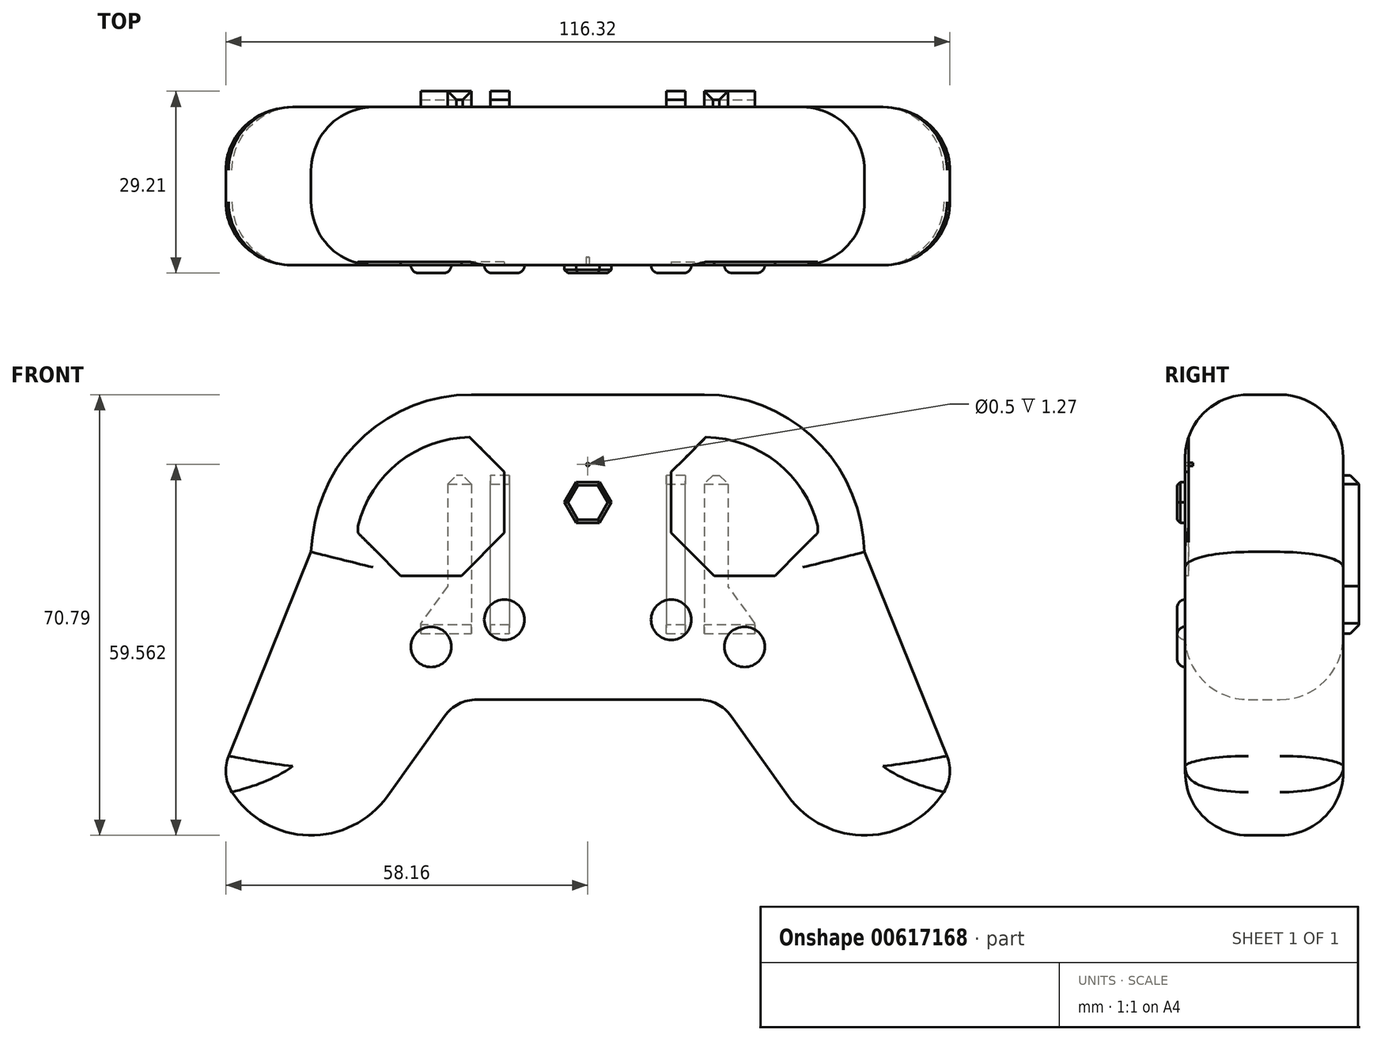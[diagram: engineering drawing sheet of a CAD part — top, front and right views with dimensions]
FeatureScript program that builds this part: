
annotation { "Feature Type Name" : "Feature", "Feature Type Description" : "" }
export const myFeature = defineFeature(function(context is Context, id is Id, definition is map)
    precondition{}
    {
        {
            var Q0;
            Q0=qCreatedBy(makeId("Front.planeOp"),FACE);
            var sketch = newSketch(context, id + "F0", { "sketchPlane" : qUnion([Q0])});
            skLineSegment(sketch, "E0", {"start": v(-44.45, 0) * mm, "end": v(44.45, 0) * mm});
            skLineSegment(sketch, "E1", {"start": v(44.45, 0) * mm, "end": v(44.45, -30.45) * mm, "construction": true});
            skLineSegment(sketch, "E2", {"start": v(-44.45, 0) * mm, "end": v(-57.7, -32.78) * mm});
            skLineSegment(sketch, "E3", {"start": v(44.45, 0) * mm, "end": v(57.7, -32.78) * mm});
            skLineSegment(sketch, "E4", {"start": v(-44.45, -30.45) * mm, "end": v(-44.45, 0) * mm, "construction": true});
            skArc(sketch, "E5", {"start": v(-57.15, -38.58) * mm, "mid": v(-44.84, -45.53) * mm, "end": v(-32.18, -39.22) * mm});
            skArc(sketch, "E6", {"start": v(32.18, -39.22) * mm, "mid": v(44.84, -45.53) * mm, "end": v(57.15, -38.58) * mm});
            skLineSegment(sketch, "E7", {"start": v(32.18, -39.22) * mm, "end": v(23, -26.38) * mm});
            skLineSegment(sketch, "E8", {"start": v(-32.18, -39.22) * mm, "end": v(-23, -26.38) * mm});
            skPoint(sketch, "E9.visualSharp", {"position": v(-58.72, -35.33) * mm});
            skArc(sketch, "E9.filletArc", {"start": v(-57.7, -32.78) * mm, "mid": v(-58.13, -35.74) * mm, "end": v(-57.15, -38.58) * mm});
            skPoint(sketch, "E10.visualSharp", {"position": v(58.72, -35.33) * mm});
            skArc(sketch, "E10.filletArc", {"start": v(57.15, -38.58) * mm, "mid": v(58.13, -35.74) * mm, "end": v(57.7, -32.78) * mm});
            skLineSegment(sketch, "E11", {"start": v(-17.83, -23.72) * mm, "end": v(17.83, -23.72) * mm});
            skPoint(sketch, "E12.visualSharp", {"position": v(-21.1, -23.72) * mm});
            skArc(sketch, "E12.filletArc", {"start": v(-17.83, -23.72) * mm, "mid": v(-20.74, -24.43) * mm, "end": v(-23, -26.38) * mm});
            skPoint(sketch, "E13.visualSharp", {"position": v(21.1, -23.72) * mm});
            skArc(sketch, "E13.filletArc", {"start": v(23, -26.38) * mm, "mid": v(20.74, -24.43) * mm, "end": v(17.83, -23.72) * mm});
            skLineSegment(sketch, "E14", {"start": v(-44.45, 0) * mm, "end": v(-44.2, 2.29) * mm});
            skLineSegment(sketch, "E15", {"start": v(44.45, 0) * mm, "end": v(44.2, 2.29) * mm});
            skLineSegment(sketch, "E16", {"start": v(-18.7, 25.26) * mm, "end": v(18.7, 25.26) * mm});
            skPoint(sketch, "E17.visualSharp", {"position": v(-41.8, 25.26) * mm});
            skArc(sketch, "E17.filletArc", {"start": v(-18.7, 25.26) * mm, "mid": v(-35.86, 18.67) * mm, "end": v(-44.2, 2.29) * mm});
            skPoint(sketch, "E18.visualSharp", {"position": v(41.8, 25.26) * mm});
            skArc(sketch, "E18.filletArc", {"start": v(44.2, 2.29) * mm, "mid": v(35.86, 18.67) * mm, "end": v(18.7, 25.26) * mm});
            skSolve(sketch);
        }
        {
            var Q0;
            Q0=makeQuery(id+"F0.imprint","IMPRINT",FACE,{"disambiguationData":[TD([[makeQuery(id+"F0.imprint","IMPRINT",EDGE,{"derivedFrom":sQuery(id+"F0.wireOp",EDGE,"E0")}),-1.0]])]});
            var Q1;
            Q1=makeQuery(id+"F0.imprint","IMPRINT",FACE,{"disambiguationData":[TD([[makeQuery(id+"F0.imprint","IMPRINT",EDGE,{"derivedFrom":sQuery(id+"F0.wireOp",EDGE,"E0")}),1.0]])]});
            extrude(context, id + "F1", {"entities" : qUnion([Q0, Q1]), "depth" : 25.4 * mm, "offsetDistance" : 25.4 * mm});
        }
        {
            var Q0;
            Q0=makeQuery(id+"F1.opExtrude","CAP_FACE",FACE,{"disambiguationData":[OSD([sQuery(id+"F0.wireOp",EDGE,"E2"),sQuery(id+"F0.wireOp",EDGE,"E3"),sQuery(id+"F0.wireOp",EDGE,"E5"),sQuery(id+"F0.wireOp",EDGE,"E6"),sQuery(id+"F0.wireOp",EDGE,"E7"),sQuery(id+"F0.wireOp",EDGE,"E8"),sQuery(id+"F0.wireOp",EDGE,"E9.filletArc"),sQuery(id+"F0.wireOp",EDGE,"E10.filletArc"),sQuery(id+"F0.wireOp",EDGE,"E11"),sQuery(id+"F0.wireOp",EDGE,"E12.filletArc"),sQuery(id+"F0.wireOp",EDGE,"E13.filletArc"),sQuery(id+"F0.wireOp",EDGE,"E14"),sQuery(id+"F0.wireOp",EDGE,"E15"),sQuery(id+"F0.wireOp",EDGE,"E16"),sQuery(id+"F0.wireOp",EDGE,"E17.filletArc"),sQuery(id+"F0.wireOp",EDGE,"E18.filletArc")])],"isStart":false});
            var sketch = newSketch(context, id + "F2", { "sketchPlane" : qUnion([Q0])});
            skArc(sketch, "E19.0.0", {"start": v(-23, -26.38) * mm, "mid": v(-20.74, -24.43) * mm, "end": v(-17.83, -23.72) * mm});
            skLineSegment(sketch, "E19.0.1", {"start": v(-17.83, -23.72) * mm, "end": v(17.83, -23.72) * mm});
            skArc(sketch, "E19.0.2", {"start": v(17.83, -23.72) * mm, "mid": v(20.74, -24.43) * mm, "end": v(23, -26.38) * mm});
            skLineSegment(sketch, "E19.0.3", {"start": v(23, -26.38) * mm, "end": v(32.18, -39.22) * mm});
            skArc(sketch, "E19.0.4", {"start": v(32.18, -39.22) * mm, "mid": v(44.84, -45.53) * mm, "end": v(57.15, -38.58) * mm});
            skArc(sketch, "E19.0.5", {"start": v(57.15, -38.58) * mm, "mid": v(58.13, -35.74) * mm, "end": v(57.7, -32.78) * mm});
            skLineSegment(sketch, "E19.0.6", {"start": v(57.7, -32.78) * mm, "end": v(44.45, 0) * mm});
            skLineSegment(sketch, "E19.0.7", {"start": v(44.45, 0) * mm, "end": v(44.2, 2.29) * mm});
            skArc(sketch, "E19.0.8", {"start": v(44.2, 2.29) * mm, "mid": v(35.86, 18.67) * mm, "end": v(18.7, 25.26) * mm});
            skLineSegment(sketch, "E19.0.9", {"start": v(18.7, 25.26) * mm, "end": v(-18.7, 25.26) * mm});
            skArc(sketch, "E19.0.10", {"start": v(-18.7, 25.26) * mm, "mid": v(-35.86, 18.67) * mm, "end": v(-44.2, 2.29) * mm});
            skLineSegment(sketch, "E19.0.11", {"start": v(-44.2, 2.29) * mm, "end": v(-44.45, 0) * mm});
            skLineSegment(sketch, "E19.0.12", {"start": v(-44.45, 0) * mm, "end": v(-57.7, -32.78) * mm});
            skArc(sketch, "E19.0.13", {"start": v(-57.7, -32.78) * mm, "mid": v(-58.13, -35.74) * mm, "end": v(-57.15, -38.58) * mm});
            skArc(sketch, "E19.0.14", {"start": v(-57.15, -38.58) * mm, "mid": v(-44.84, -45.53) * mm, "end": v(-32.18, -39.22) * mm});
            skLineSegment(sketch, "E19.0.15", {"start": v(-32.18, -39.22) * mm, "end": v(-23, -26.38) * mm});
            skLineSegment(sketch, "E20", {"start": v(-25.17, 24.43) * mm, "end": v(-25.17, 19.73) * mm});
            skLineSegment(sketch, "E21", {"start": v(-44.45, 0) * mm, "end": v(44.45, 0) * mm});
            skLineSegment(sketch, "E22", {"start": v(25.17, 24.43) * mm, "end": v(25.17, 19.73) * mm});
            skLineSegment(sketch, "E23.0", {"start": v(-30.05, 19.73) * mm, "end": v(-20.3, 19.73) * mm});
            skLineSegment(sketch, "E23.1", {"start": v(-20.3, 19.73) * mm, "end": v(-13.4, 12.83) * mm});
            skLineSegment(sketch, "E23.2", {"start": v(-13.4, 12.83) * mm, "end": v(-13.4, 3.08) * mm});
            skLineSegment(sketch, "E23.3", {"start": v(-13.4, 3.08) * mm, "end": v(-20.3, -3.82) * mm});
            skLineSegment(sketch, "E23.4", {"start": v(-20.3, -3.82) * mm, "end": v(-30.05, -3.82) * mm});
            skLineSegment(sketch, "E23.5", {"start": v(-30.05, -3.82) * mm, "end": v(-36.95, 3.08) * mm});
            skLineSegment(sketch, "E23.6", {"start": v(-36.95, 3.08) * mm, "end": v(-36.95, 12.83) * mm});
            skLineSegment(sketch, "E23.7", {"start": v(-36.95, 12.83) * mm, "end": v(-30.05, 19.73) * mm});
            skPoint(sketch, "E23.0.midPoint", {"position": v(-25.17, 19.73) * mm});
            skPoint(sketch, "E24.cCircle.centerSnap0", {"position": v(-13.4, 7.95) * mm});
            skLineSegment(sketch, "E24.0", {"start": v(20.3, 19.73) * mm, "end": v(30.05, 19.73) * mm});
            skLineSegment(sketch, "E24.1", {"start": v(30.05, 19.73) * mm, "end": v(36.95, 12.83) * mm});
            skLineSegment(sketch, "E24.2", {"start": v(36.95, 12.83) * mm, "end": v(36.95, 3.08) * mm});
            skLineSegment(sketch, "E24.3", {"start": v(36.95, 3.08) * mm, "end": v(30.05, -3.82) * mm});
            skLineSegment(sketch, "E24.4", {"start": v(30.05, -3.82) * mm, "end": v(20.3, -3.82) * mm});
            skLineSegment(sketch, "E24.5", {"start": v(20.3, -3.82) * mm, "end": v(13.4, 3.08) * mm});
            skLineSegment(sketch, "E24.6", {"start": v(13.4, 3.08) * mm, "end": v(13.4, 12.83) * mm});
            skLineSegment(sketch, "E24.7", {"start": v(13.4, 12.83) * mm, "end": v(20.3, 19.73) * mm});
            skPoint(sketch, "E24.0.midPoint", {"position": v(25.17, 19.73) * mm});
            skLineSegment(sketch, "E25", {"start": v(-20.3, -3.82) * mm, "end": v(-30.05, 19.73) * mm});
            skLineSegment(sketch, "E26", {"start": v(-30.05, -3.82) * mm, "end": v(-20.3, 19.73) * mm});
            skLineSegment(sketch, "E27", {"start": v(-13.4, 12.83) * mm, "end": v(-36.95, 3.08) * mm});
            skLineSegment(sketch, "E28", {"start": v(-36.95, 12.83) * mm, "end": v(-13.4, 3.08) * mm});
            skLineSegment(sketch, "E29", {"start": v(13.4, 12.83) * mm, "end": v(36.95, 3.08) * mm});
            skLineSegment(sketch, "E30", {"start": v(13.4, 3.08) * mm, "end": v(36.95, 12.83) * mm});
            skLineSegment(sketch, "E31", {"start": v(20.3, 19.73) * mm, "end": v(30.05, -3.82) * mm});
            skLineSegment(sketch, "E32", {"start": v(20.3, -3.82) * mm, "end": v(30.05, 19.73) * mm});
            skLineSegment(sketch, "E33", {"start": v(-13.4, 3.08) * mm, "end": v(-13.4, -10.9) * mm, "construction": true});
            skLineSegment(sketch, "E34", {"start": v(-25.17, -3.82) * mm, "end": v(-25.17, -15.25) * mm, "construction": true});
            skCircle(sketch, "E35", {"center": v(-25.17, -15.25) * mm, "radius": 3.24 * mm});
            skCircle(sketch, "E36", {"center": v(-13.4, -10.9) * mm, "radius": 3.24 * mm});
            skLineSegment(sketch, "E37", {"start": v(13.4, 3.08) * mm, "end": v(13.4, -10.9) * mm, "construction": true});
            skLineSegment(sketch, "E38", {"start": v(25.17, -3.82) * mm, "end": v(25.17, -15.25) * mm, "construction": true});
            skCircle(sketch, "E39", {"center": v(13.4, -10.9) * mm, "radius": 3.24 * mm});
            skCircle(sketch, "E40", {"center": v(25.17, -15.25) * mm, "radius": 3.24 * mm});
            skLineSegment(sketch, "E41", {"start": v(-13.4, 7.95) * mm, "end": v(13.4, 7.95) * mm});
            skCircle(sketch, "E42.cCircle", {"center": v(0, 7.95) * mm, "radius": 3.27 * mm, "construction": true});
            skLineSegment(sketch, "E42.0", {"start": v(-1.89, 11.22) * mm, "end": v(1.89, 11.22) * mm});
            skLineSegment(sketch, "E42.1", {"start": v(1.89, 11.22) * mm, "end": v(3.77, 7.95) * mm});
            skLineSegment(sketch, "E42.2", {"start": v(3.77, 7.95) * mm, "end": v(1.89, 4.69) * mm});
            skLineSegment(sketch, "E42.3", {"start": v(1.89, 4.69) * mm, "end": v(-1.89, 4.69) * mm});
            skLineSegment(sketch, "E42.4", {"start": v(-1.89, 4.69) * mm, "end": v(-3.77, 7.95) * mm});
            skLineSegment(sketch, "E42.5", {"start": v(-3.77, 7.95) * mm, "end": v(-1.89, 11.22) * mm});
            skPoint(sketch, "E42.0.midPoint", {"position": v(0, 11.22) * mm});
            skLineSegment(sketch, "E43", {"start": v(0, 11.22) * mm, "end": v(0, 14.03) * mm});
            skCircle(sketch, "E44", {"center": v(0, 14.03) * mm, "radius": 0.25 * mm});
            skSolve(sketch);
        }
        {
            var Q0;
            Q0=makeQuery(id+"F2.imprint","IMPRINT",FACE,{"disambiguationData":[TD([[makeQuery(id+"F2.imprint","IMPRINT",EDGE,{"derivedFrom":sQuery(id+"F2.wireOp",EDGE,"E35")}),1.0]])]});
            var Q1;
            Q1=makeQuery(id+"F2.imprint","IMPRINT",FACE,{"disambiguationData":[TD([[makeQuery(id+"F2.imprint","IMPRINT",EDGE,{"derivedFrom":sQuery(id+"F2.wireOp",EDGE,"E36")}),1.0]])]});
            var Q2;
            Q2=makeQuery(id+"F2.imprint","IMPRINT",FACE,{"disambiguationData":[TD([[makeQuery(id+"F2.imprint","IMPRINT",EDGE,{"derivedFrom":sQuery(id+"F2.wireOp",EDGE,"E39")}),1.0]])]});
            var Q3;
            Q3=makeQuery(id+"F2.imprint","IMPRINT",FACE,{"disambiguationData":[TD([[makeQuery(id+"F2.imprint","IMPRINT",EDGE,{"derivedFrom":sQuery(id+"F2.wireOp",EDGE,"E40")}),1.0]])]});
            var Q4;
            {var subQ0=sQuery(id+"F2.wireOp",EDGE,"E42.2");Q4=makeQuery(id+"F2.imprint","IMPRINT",FACE,{"disambiguationData":[TD([[makeQuery(id+"F2.imprint","IMPRINT",EDGE,{"derivedFrom":subQ0}),-1.0]])]});}
            var Q5;
            Q5=makeQuery(id+"F2.imprint","IMPRINT",FACE,{"disambiguationData":[TD([[makeQuery(id+"F2.imprint","IMPRINT",EDGE,{"derivedFrom":sQuery(id+"F2.wireOp",EDGE,"E42.0")}),-1.0]])]});
            extrude(context, id + "F3", {"entities" : qUnion([Q0, Q1, Q2, Q3, Q4, Q5]), "depth" : 1.27 * mm, "offsetDistance" : 25.4 * mm});
        }
        {
            var Q0;
            {var subQ0=sQuery(id+"F2.wireOp",EDGE,"E25");var subQ1=sQuery(id+"F2.wireOp",EDGE,"E21");var subQ2=makeQuery(id+"F2.imprint","INTERSECT",VERTEX,{"derivedFrom":[subQ1,subQ0]});Q0=makeQuery(id+"F2.imprint","IMPRINT",FACE,{"disambiguationData":[TD([[makeQuery(id+"F2.imprint","IMPRINT",EDGE,{"disambiguationData":[TD([[subQ2,-1.0]])],"derivedFrom":subQ1}),1.0]])]});}
            var Q1;
            {var subQ0=sQuery(id+"F2.wireOp",EDGE,"E25");var subQ1=sQuery(id+"F2.wireOp",EDGE,"E21");var subQ2=makeQuery(id+"F2.imprint","INTERSECT",VERTEX,{"derivedFrom":[subQ1,subQ0]});Q1=makeQuery(id+"F2.imprint","IMPRINT",FACE,{"disambiguationData":[TD([[makeQuery(id+"F2.imprint","IMPRINT",EDGE,{"disambiguationData":[TD([[subQ2,-1.0]])],"derivedFrom":subQ1}),-1.0]])]});}
            var Q2;
            {var subQ5=sQuery(id+"F2.wireOp",EDGE,"E23.4");Q2=makeQuery(id+"F2.imprint","IMPRINT",FACE,{"disambiguationData":[TD([[makeQuery(id+"F2.imprint","IMPRINT",EDGE,{"derivedFrom":subQ5}),-1.0]])]});}
            var Q3;
            {var subQ0=sQuery(id+"F2.wireOp",EDGE,"E23.5");var subQ1=sQuery(id+"F2.wireOp",EDGE,"E21");var subQ2=makeQuery(id+"F2.imprint","INTERSECT",VERTEX,{"derivedFrom":[subQ1,subQ0]});Q3=makeQuery(id+"F2.imprint","IMPRINT",FACE,{"disambiguationData":[TD([[makeQuery(id+"F2.imprint","IMPRINT",EDGE,{"disambiguationData":[TD([[subQ2,-1.0]])],"derivedFrom":subQ1}),-1.0]])]});}
            var Q4;
            {var subQ0=sQuery(id+"F2.wireOp",EDGE,"E23.5");var subQ1=sQuery(id+"F2.wireOp",EDGE,"E21");var subQ2=makeQuery(id+"F2.imprint","INTERSECT",VERTEX,{"derivedFrom":[subQ1,subQ0]});Q4=makeQuery(id+"F2.imprint","IMPRINT",FACE,{"disambiguationData":[TD([[makeQuery(id+"F2.imprint","IMPRINT",EDGE,{"disambiguationData":[TD([[subQ2,-1.0]])],"derivedFrom":subQ1}),1.0]])]});}
            var Q5;
            {var subQ0=sQuery(id+"F2.wireOp",EDGE,"E23.6");Q5=makeQuery(id+"F2.imprint","IMPRINT",FACE,{"disambiguationData":[TD([[makeQuery(id+"F2.imprint","IMPRINT",EDGE,{"derivedFrom":subQ0}),-1.0]])]});}
            var Q6;
            {var subQ0=sQuery(id+"F2.wireOp",EDGE,"E23.7");Q6=makeQuery(id+"F2.imprint","IMPRINT",FACE,{"disambiguationData":[TD([[makeQuery(id+"F2.imprint","IMPRINT",EDGE,{"derivedFrom":subQ0}),-1.0]])]});}
            var Q7;
            {var subQ0=sQuery(id+"F2.wireOp",EDGE,"E23.0");var subQ1=makeQuery(id+"F2.imprint","INTERSECT",VERTEX,{"derivedFrom":[sQuery(id+"F2.wireOp",EDGE,"E20"),subQ0]});Q7=makeQuery(id+"F2.imprint","IMPRINT",FACE,{"disambiguationData":[TD([[makeQuery(id+"F2.imprint","IMPRINT",EDGE,{"disambiguationData":[TD([[subQ1,1.0]])],"derivedFrom":subQ0}),-1.0]])]});}
            var Q8;
            {var subQ0=sQuery(id+"F2.wireOp",EDGE,"E23.1");Q8=makeQuery(id+"F2.imprint","IMPRINT",FACE,{"disambiguationData":[TD([[makeQuery(id+"F2.imprint","IMPRINT",EDGE,{"derivedFrom":subQ0}),-1.0]])]});}
            var Q9;
            {var subQ1=sQuery(id+"F2.wireOp",EDGE,"E23.2");var subQ3=makeQuery(id+"F2.imprint","INTERSECT",VERTEX,{"derivedFrom":[subQ1,sQuery(id+"F2.wireOp",EDGE,"E41")]});Q9=makeQuery(id+"F2.imprint","IMPRINT",FACE,{"disambiguationData":[TD([[makeQuery(id+"F2.imprint","IMPRINT",EDGE,{"disambiguationData":[TD([[subQ3,1.0]])],"derivedFrom":subQ1}),-1.0]])]});}
            var Q10;
            {var subQ1=sQuery(id+"F2.wireOp",EDGE,"E24.6");var subQ3=makeQuery(id+"F2.imprint","INTERSECT",VERTEX,{"derivedFrom":[subQ1,sQuery(id+"F2.wireOp",EDGE,"E41")]});Q10=makeQuery(id+"F2.imprint","IMPRINT",FACE,{"disambiguationData":[TD([[makeQuery(id+"F2.imprint","IMPRINT",EDGE,{"disambiguationData":[TD([[subQ3,1.0]])],"derivedFrom":subQ1}),-1.0]])]});}
            var Q11;
            {var subQ0=sQuery(id+"F2.wireOp",EDGE,"E24.5");var subQ1=sQuery(id+"F2.wireOp",EDGE,"E21");var subQ2=makeQuery(id+"F2.imprint","INTERSECT",VERTEX,{"derivedFrom":[subQ1,subQ0]});Q11=makeQuery(id+"F2.imprint","IMPRINT",FACE,{"disambiguationData":[TD([[makeQuery(id+"F2.imprint","IMPRINT",EDGE,{"disambiguationData":[TD([[subQ2,-1.0]])],"derivedFrom":subQ1}),1.0]])]});}
            var Q12;
            {var subQ0=sQuery(id+"F2.wireOp",EDGE,"E32");var subQ1=sQuery(id+"F2.wireOp",EDGE,"E21");var subQ2=makeQuery(id+"F2.imprint","INTERSECT",VERTEX,{"derivedFrom":[subQ1,subQ0]});Q12=makeQuery(id+"F2.imprint","IMPRINT",FACE,{"disambiguationData":[TD([[makeQuery(id+"F2.imprint","IMPRINT",EDGE,{"disambiguationData":[TD([[subQ2,-1.0]])],"derivedFrom":subQ1}),1.0]])]});}
            var Q13;
            {var subQ0=sQuery(id+"F2.wireOp",EDGE,"E31");var subQ1=sQuery(id+"F2.wireOp",EDGE,"E21");var subQ2=makeQuery(id+"F2.imprint","INTERSECT",VERTEX,{"derivedFrom":[subQ1,subQ0]});Q13=makeQuery(id+"F2.imprint","IMPRINT",FACE,{"disambiguationData":[TD([[makeQuery(id+"F2.imprint","IMPRINT",EDGE,{"disambiguationData":[TD([[subQ2,-1.0]])],"derivedFrom":subQ1}),1.0]])]});}
            var Q14;
            {var subQ0=sQuery(id+"F2.wireOp",EDGE,"E24.2");Q14=makeQuery(id+"F2.imprint","IMPRINT",FACE,{"disambiguationData":[TD([[makeQuery(id+"F2.imprint","IMPRINT",EDGE,{"derivedFrom":subQ0}),-1.0]])]});}
            var Q15;
            {var subQ0=sQuery(id+"F2.wireOp",EDGE,"E24.1");Q15=makeQuery(id+"F2.imprint","IMPRINT",FACE,{"disambiguationData":[TD([[makeQuery(id+"F2.imprint","IMPRINT",EDGE,{"derivedFrom":subQ0}),-1.0]])]});}
            var Q16;
            {var subQ0=sQuery(id+"F2.wireOp",EDGE,"E24.0");var subQ1=makeQuery(id+"F2.imprint","INTERSECT",VERTEX,{"derivedFrom":[sQuery(id+"F2.wireOp",EDGE,"E22"),subQ0]});Q16=makeQuery(id+"F2.imprint","IMPRINT",FACE,{"disambiguationData":[TD([[makeQuery(id+"F2.imprint","IMPRINT",EDGE,{"disambiguationData":[TD([[subQ1,1.0]])],"derivedFrom":subQ0}),-1.0]])]});}
            var Q17;
            {var subQ0=sQuery(id+"F2.wireOp",EDGE,"E24.7");Q17=makeQuery(id+"F2.imprint","IMPRINT",FACE,{"disambiguationData":[TD([[makeQuery(id+"F2.imprint","IMPRINT",EDGE,{"derivedFrom":subQ0}),-1.0]])]});}
            var Q18;
            {var subQ5=sQuery(id+"F2.wireOp",EDGE,"E24.4");Q18=makeQuery(id+"F2.imprint","IMPRINT",FACE,{"disambiguationData":[TD([[makeQuery(id+"F2.imprint","IMPRINT",EDGE,{"derivedFrom":subQ5}),-1.0]])]});}
            var Q19;
            {var subQ0=sQuery(id+"F2.wireOp",EDGE,"E31");var subQ1=sQuery(id+"F2.wireOp",EDGE,"E21");var subQ2=makeQuery(id+"F2.imprint","INTERSECT",VERTEX,{"derivedFrom":[subQ1,subQ0]});Q19=makeQuery(id+"F2.imprint","IMPRINT",FACE,{"disambiguationData":[TD([[makeQuery(id+"F2.imprint","IMPRINT",EDGE,{"disambiguationData":[TD([[subQ2,-1.0]])],"derivedFrom":subQ1}),-1.0]])]});}
            var Q20;
            {var subQ0=sQuery(id+"F2.wireOp",EDGE,"E24.5");var subQ1=sQuery(id+"F2.wireOp",EDGE,"E21");var subQ2=makeQuery(id+"F2.imprint","INTERSECT",VERTEX,{"derivedFrom":[subQ1,subQ0]});Q20=makeQuery(id+"F2.imprint","IMPRINT",FACE,{"disambiguationData":[TD([[makeQuery(id+"F2.imprint","IMPRINT",EDGE,{"disambiguationData":[TD([[subQ2,-1.0]])],"derivedFrom":subQ1}),-1.0]])]});}
            var Q21;
            {var subQ0=sQuery(id+"F2.wireOp",EDGE,"E26");var subQ1=sQuery(id+"F2.wireOp",EDGE,"E21");var subQ2=makeQuery(id+"F2.imprint","INTERSECT",VERTEX,{"derivedFrom":[subQ1,subQ0]});Q21=makeQuery(id+"F2.imprint","IMPRINT",FACE,{"disambiguationData":[TD([[makeQuery(id+"F2.imprint","IMPRINT",EDGE,{"disambiguationData":[TD([[subQ2,-1.0]])],"derivedFrom":subQ1}),1.0]])]});}
            extrude(context, id + "F4", {"entities" : qUnion([Q0, Q1, Q2, Q3, Q4, Q5, Q6, Q7, Q8, Q9, Q10, Q11, Q12, Q13, Q14, Q15, Q16, Q17, Q18, Q19, Q20, Q21]), "operationType" : NewBodyOperationType.REMOVE, "oppositeDirection" : true, "depth" : 0.56 * mm, "offsetDistance" : 25.4 * mm});
        }
        {
            var Q0;
            Q0=makeQuery(id+"F1.opExtrude","CAP_EDGE",EDGE,{"disambiguationData":[OSD([sQuery(id+"F0.wireOp",EDGE,"E18.filletArc")])],"isStart":false});
            var Q1;
            Q1=makeQuery(id+"F1.opExtrude","CAP_EDGE",EDGE,{"disambiguationData":[OSD([sQuery(id+"F0.wireOp",EDGE,"E3")])],"isStart":false});
            var Q2;
            Q2=makeQuery(id+"F1.opExtrude","CAP_EDGE",EDGE,{"disambiguationData":[OSD([sQuery(id+"F0.wireOp",EDGE,"E18.filletArc")])],"isStart":true});
            var Q3;
            Q3=makeQuery(id+"F1.opExtrude","CAP_EDGE",EDGE,{"disambiguationData":[OSD([sQuery(id+"F0.wireOp",EDGE,"E3")])],"isStart":true});
            fillet(context, id + "F5", {"entities" : qUnion([Q0, Q1, Q2, Q3]), "radius" : 10.16 * mm, "tangentPropagation" : true, "allowEdgeOverflow" : false});
        }
        {
            var Q0;
            Q0=makeQuery(id+"F2.imprint","IMPRINT",FACE,{"disambiguationData":[TD([[makeQuery(id+"F2.imprint","IMPRINT",EDGE,{"derivedFrom":sQuery(id+"F2.wireOp",EDGE,"E44")}),1.0]])]});
            extrude(context, id + "F6", {"entities" : qUnion([Q0]), "operationType" : NewBodyOperationType.REMOVE, "oppositeDirection" : true, "depth" : 1.27 * mm, "offsetDistance" : 25.4 * mm});
        }
        {
            var Q0;
            Q0=makeQuery(id+"F3.opExtrude","CAP_EDGE",EDGE,{"disambiguationData":[OSD([sQuery(id+"F2.wireOp",EDGE,"E36")])],"isStart":false});
            var Q1;
            Q1=makeQuery(id+"F3.opExtrude","CAP_EDGE",EDGE,{"disambiguationData":[OSD([sQuery(id+"F2.wireOp",EDGE,"E35")])],"isStart":false});
            var Q2;
            Q2=makeQuery(id+"F3.opExtrude","CAP_EDGE",EDGE,{"disambiguationData":[OSD([sQuery(id+"F2.wireOp",EDGE,"E39")])],"isStart":false});
            var Q3;
            Q3=makeQuery(id+"F3.opExtrude","CAP_EDGE",EDGE,{"disambiguationData":[OSD([sQuery(id+"F2.wireOp",EDGE,"E40")])],"isStart":false});
            fillet(context, id + "F7", {"entities" : qUnion([Q0, Q1, Q2, Q3]), "radius" : 1.27 * mm, "tangentPropagation" : true, "allowEdgeOverflow" : false});
        }
        {
            var Q0;
            Q0=makeQuery(id+"F3.opExtrude","CAP_EDGE",EDGE,{"disambiguationData":[OSD([sQuery(id+"F2.wireOp",EDGE,"E42.3")])],"isStart":false});
            var Q1;
            Q1=makeQuery(id+"F3.opExtrude","CAP_EDGE",EDGE,{"disambiguationData":[OSD([sQuery(id+"F2.wireOp",EDGE,"E42.2")])],"isStart":false});
            var Q2;
            Q2=makeQuery(id+"F3.opExtrude","CAP_EDGE",EDGE,{"disambiguationData":[OSD([sQuery(id+"F2.wireOp",EDGE,"E42.1")])],"isStart":false});
            var Q3;
            Q3=makeQuery(id+"F3.opExtrude","CAP_EDGE",EDGE,{"disambiguationData":[OSD([sQuery(id+"F2.wireOp",EDGE,"E42.4")])],"isStart":false});
            var Q4;
            Q4=makeQuery(id+"F3.opExtrude","CAP_EDGE",EDGE,{"disambiguationData":[OSD([sQuery(id+"F2.wireOp",EDGE,"E42.5")])],"isStart":false});
            var Q5;
            Q5=makeQuery(id+"F3.opExtrude","CAP_EDGE",EDGE,{"disambiguationData":[OSD([sQuery(id+"F2.wireOp",EDGE,"E42.0")])],"isStart":false});
            chamfer(context, id + "F8", {"entities" : qUnion([Q0, Q1, Q2, Q3, Q4, Q5]), "width" : 0.5 * mm, "tangentPropagation" : true});
        }
        {
            var Q0;
            Q0=makeQuery(id+"F1.opExtrude","CAP_FACE",FACE,{"disambiguationData":[OSD([sQuery(id+"F0.wireOp",EDGE,"E2"),sQuery(id+"F0.wireOp",EDGE,"E3"),sQuery(id+"F0.wireOp",EDGE,"E5"),sQuery(id+"F0.wireOp",EDGE,"E6"),sQuery(id+"F0.wireOp",EDGE,"E7"),sQuery(id+"F0.wireOp",EDGE,"E8"),sQuery(id+"F0.wireOp",EDGE,"E9.filletArc"),sQuery(id+"F0.wireOp",EDGE,"E10.filletArc"),sQuery(id+"F0.wireOp",EDGE,"E11"),sQuery(id+"F0.wireOp",EDGE,"E12.filletArc"),sQuery(id+"F0.wireOp",EDGE,"E13.filletArc"),sQuery(id+"F0.wireOp",EDGE,"E14"),sQuery(id+"F0.wireOp",EDGE,"E15"),sQuery(id+"F0.wireOp",EDGE,"E16"),sQuery(id+"F0.wireOp",EDGE,"E17.filletArc"),sQuery(id+"F0.wireOp",EDGE,"E18.filletArc")])],"isStart":true});
            var sketch = newSketch(context, id + "F9", { "sketchPlane" : qUnion([Q0])});
            skLineSegment(sketch, "E45.0.0", {"start": v(48.27, -36.58) * mm, "end": v(34.5, -2.48) * mm});
            skLineSegment(sketch, "E45.0.1", {"start": v(34.5, -2.48) * mm, "end": v(34.1, 1.23) * mm});
            skArc(sketch, "E45.0.2", {"start": v(34.1, 1.23) * mm, "mid": v(29.06, 11.12) * mm, "end": v(18.7, 15.1) * mm});
            skLineSegment(sketch, "E45.0.3", {"start": v(18.7, 15.1) * mm, "end": v(-18.7, 15.1) * mm});
            skArc(sketch, "E45.0.4", {"start": v(-18.7, 15.1) * mm, "mid": v(-29.06, 11.12) * mm, "end": v(-34.1, 1.23) * mm});
            skLineSegment(sketch, "E45.0.5", {"start": v(-34.1, 1.23) * mm, "end": v(-34.5, -2.48) * mm});
            skLineSegment(sketch, "E45.0.6", {"start": v(-34.5, -2.48) * mm, "end": v(-48.27, -36.58) * mm});
            skArc(sketch, "E45.0.7", {"start": v(-48.27, -36.58) * mm, "mid": v(-46.7, -34.68) * mm, "end": v(-48.6, -33.1) * mm});
            skArc(sketch, "E45.0.8", {"start": v(-48.6, -33.1) * mm, "mid": v(-44.58, -35.37) * mm, "end": v(-40.45, -33.31) * mm});
            skLineSegment(sketch, "E45.0.9", {"start": v(-40.45, -33.31) * mm, "end": v(-31.26, -20.47) * mm});
            skArc(sketch, "E45.0.10", {"start": v(-31.26, -20.47) * mm, "mid": v(-25.39, -15.4) * mm, "end": v(-17.83, -13.56) * mm});
            skLineSegment(sketch, "E45.0.11", {"start": v(-17.83, -13.56) * mm, "end": v(17.83, -13.56) * mm});
            skArc(sketch, "E45.0.12", {"start": v(17.83, -13.56) * mm, "mid": v(25.39, -15.4) * mm, "end": v(31.26, -20.47) * mm});
            skLineSegment(sketch, "E45.0.13", {"start": v(31.26, -20.47) * mm, "end": v(40.45, -33.31) * mm});
            skArc(sketch, "E45.0.14", {"start": v(40.45, -33.31) * mm, "mid": v(44.58, -35.37) * mm, "end": v(48.6, -33.1) * mm});
            skArc(sketch, "E45.0.15", {"start": v(48.6, -33.1) * mm, "mid": v(46.7, -34.68) * mm, "end": v(48.27, -36.58) * mm});
            skLineSegment(sketch, "E46", {"start": v(-18.7, 12.3) * mm, "end": v(-18.7, -13.1) * mm});
            skLineSegment(sketch, "E47", {"start": v(18.7, 12.3) * mm, "end": v(18.7, -13.1) * mm});
            skLineSegment(sketch, "E48", {"start": v(-18.7, 12.3) * mm, "end": v(-22.5, 12.3) * mm});
            skLineSegment(sketch, "E49", {"start": v(-22.5, 12.3) * mm, "end": v(-22.5, -5.47) * mm});
            skLineSegment(sketch, "E50", {"start": v(-18.7, -13.1) * mm, "end": v(-26.82, -13.1) * mm});
            skLineSegment(sketch, "E51", {"start": v(-26.82, -13.1) * mm, "end": v(-26.82, -11.44) * mm});
            skLineSegment(sketch, "E52", {"start": v(-26.82, -11.44) * mm, "end": v(-22.5, -5.47) * mm});
            skLineSegment(sketch, "E53", {"start": v(18.7, 12.3) * mm, "end": v(22.5, 12.3) * mm});
            skLineSegment(sketch, "E54", {"start": v(22.5, 12.3) * mm, "end": v(22.5, -5.47) * mm});
            skLineSegment(sketch, "E55", {"start": v(22.5, -5.47) * mm, "end": v(26.82, -11.44) * mm});
            skLineSegment(sketch, "E56", {"start": v(18.7, -13.1) * mm, "end": v(26.82, -13.1) * mm});
            skLineSegment(sketch, "E57", {"start": v(26.82, -13.1) * mm, "end": v(26.82, -11.44) * mm});
            skLineSegment(sketch, "E58", {"start": v(-15.65, -13.1) * mm, "end": v(-15.65, 12.3) * mm});
            skLineSegment(sketch, "E59", {"start": v(-15.65, 12.3) * mm, "end": v(-12.6, 12.3) * mm});
            skLineSegment(sketch, "E60", {"start": v(-12.6, 12.3) * mm, "end": v(-12.6, -13.1) * mm});
            skLineSegment(sketch, "E61", {"start": v(-12.6, -13.1) * mm, "end": v(-15.65, -13.1) * mm});
            skLineSegment(sketch, "E62", {"start": v(15.65, -13.1) * mm, "end": v(15.65, 12.3) * mm});
            skLineSegment(sketch, "E63", {"start": v(15.65, 12.3) * mm, "end": v(12.6, 12.3) * mm});
            skLineSegment(sketch, "E64", {"start": v(12.6, 12.3) * mm, "end": v(12.6, -13.1) * mm});
            skLineSegment(sketch, "E65", {"start": v(12.6, -13.1) * mm, "end": v(15.65, -13.1) * mm});
            skSolve(sketch);
        }
        {
            var Q0;
            Q0=makeQuery(id+"F9.imprint","IMPRINT",FACE,{"disambiguationData":[TD([[makeQuery(id+"F9.imprint","IMPRINT",EDGE,{"derivedFrom":sQuery(id+"F9.wireOp",EDGE,"E46")}),-1.0]])]});
            var Q1;
            Q1=makeQuery(id+"F9.imprint","IMPRINT",FACE,{"disambiguationData":[TD([[makeQuery(id+"F9.imprint","IMPRINT",EDGE,{"derivedFrom":sQuery(id+"F9.wireOp",EDGE,"E58")}),-1.0]])]});
            var Q2;
            Q2=makeQuery(id+"F9.imprint","IMPRINT",FACE,{"disambiguationData":[TD([[makeQuery(id+"F9.imprint","IMPRINT",EDGE,{"derivedFrom":sQuery(id+"F9.wireOp",EDGE,"E62")}),1.0]])]});
            var Q3;
            Q3=makeQuery(id+"F9.imprint","IMPRINT",FACE,{"disambiguationData":[TD([[makeQuery(id+"F9.imprint","IMPRINT",EDGE,{"derivedFrom":sQuery(id+"F9.wireOp",EDGE,"E47")}),1.0]])]});
            extrude(context, id + "F10", {"entities" : qUnion([Q0, Q1, Q2, Q3]), "depth" : 2.54 * mm, "offsetDistance" : 25.4 * mm});
        }
        {
            var Q0;
            Q0=makeQuery(id+"F10.opExtrude","CAP_EDGE",EDGE,{"disambiguationData":[OSD([sQuery(id+"F9.wireOp",EDGE,"E59")])],"isStart":false});
            var Q1;
            Q1=makeQuery(id+"F10.opExtrude","CAP_EDGE",EDGE,{"disambiguationData":[OSD([sQuery(id+"F9.wireOp",EDGE,"E63")])],"isStart":false});
            var Q2;
            Q2=makeQuery(id+"F10.opExtrude","CAP_EDGE",EDGE,{"disambiguationData":[OSD([sQuery(id+"F9.wireOp",EDGE,"E53")])],"isStart":false});
            var Q3;
            Q3=makeQuery(id+"F10.opExtrude","CAP_EDGE",EDGE,{"disambiguationData":[OSD([sQuery(id+"F9.wireOp",EDGE,"E48")])],"isStart":false});
            var Q4;
            Q4=makeQuery(id+"F10.opExtrude","SWEPT_EDGE",EDGE,{"disambiguationData":[OSD([sQuery(id+"F9.wireOp",EDGE,"E46"),sQuery(id+"F9.wireOp",EDGE,"E48")])]});
            var Q5;
            Q5=makeQuery(id+"F10.opExtrude","SWEPT_EDGE",EDGE,{"disambiguationData":[OSD([sQuery(id+"F9.wireOp",EDGE,"E48"),sQuery(id+"F9.wireOp",EDGE,"E49")])]});
            var Q6;
            Q6=makeQuery(id+"F10.opExtrude","SWEPT_EDGE",EDGE,{"disambiguationData":[OSD([sQuery(id+"F9.wireOp",EDGE,"E53"),sQuery(id+"F9.wireOp",EDGE,"E54")])]});
            var Q7;
            Q7=makeQuery(id+"F10.opExtrude","SWEPT_EDGE",EDGE,{"disambiguationData":[OSD([sQuery(id+"F9.wireOp",EDGE,"E47"),sQuery(id+"F9.wireOp",EDGE,"E53")])]});
            var Q8;
            Q8=makeQuery(id+"F10.opExtrude","CAP_EDGE",EDGE,{"disambiguationData":[OSD([sQuery(id+"F9.wireOp",EDGE,"E61")])],"isStart":false});
            var Q9;
            Q9=makeQuery(id+"F10.opExtrude","CAP_EDGE",EDGE,{"disambiguationData":[OSD([sQuery(id+"F9.wireOp",EDGE,"E50")])],"isStart":false});
            var Q10;
            Q10=makeQuery(id+"F10.opExtrude","CAP_EDGE",EDGE,{"disambiguationData":[OSD([sQuery(id+"F9.wireOp",EDGE,"E56")])],"isStart":false});
            var Q11;
            Q11=makeQuery(id+"F10.opExtrude","CAP_EDGE",EDGE,{"disambiguationData":[OSD([sQuery(id+"F9.wireOp",EDGE,"E65")])],"isStart":false});
            chamfer(context, id + "F11", {"entities" : qUnion([Q0, Q1, Q2, Q3, Q4, Q5, Q6, Q7, Q8, Q9, Q10, Q11]), "width" : 1.4 * mm, "tangentPropagation" : true});
        }
    });
